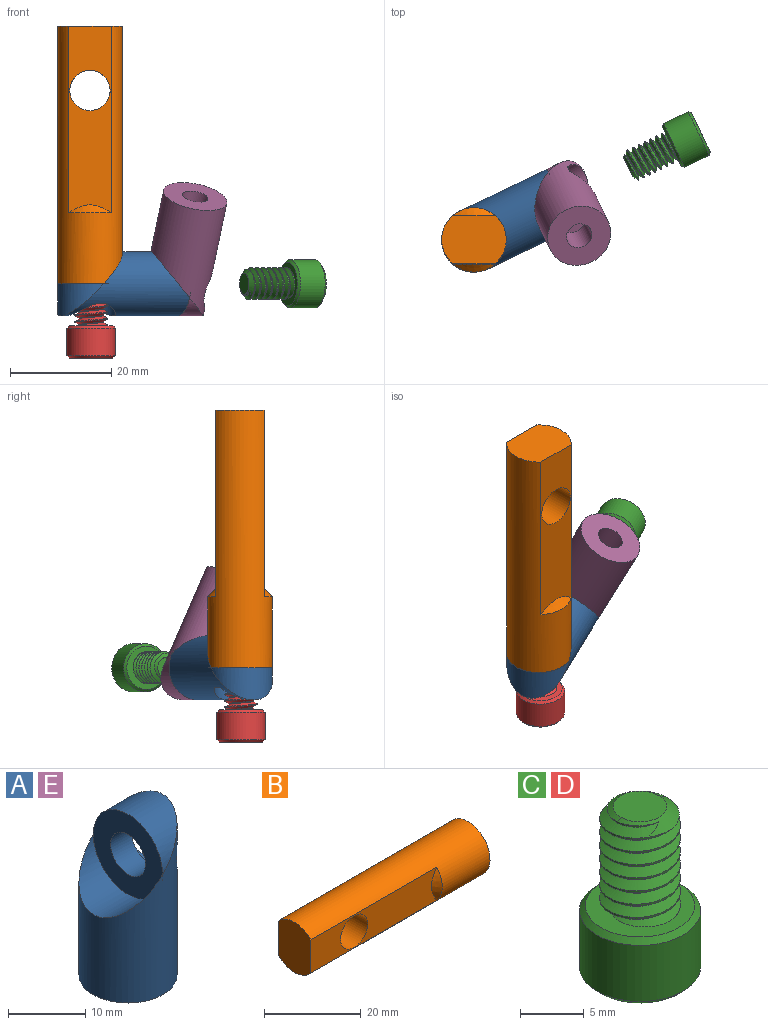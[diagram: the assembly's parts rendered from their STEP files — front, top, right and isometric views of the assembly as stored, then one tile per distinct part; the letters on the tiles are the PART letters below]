
ASSEMBLY  parts=5 mates=4
PART A: 12 faces, bbox 12.7x12.7x25.4 mm
  f0: cylinder r=3.17mm len=6.35mm, axis (-1,0,0), area 76mm2, adj f5,f9
  f1: cylinder r=6.35mm len=25.42mm, axis (0,0,-1), area 670.1mm2, adj f2,f3,f4,f5,f6,f7,f8
  f2: plane 12.7x12.7mm, normal (0,0,-1), area 106.2mm2, adj f1,f10
  f3: cylinder r=6.35mm len=12.7mm, axis (-1,0,0), area 80.6mm2, adj f1,f4,f5
  f4: plane 0.02x0mm, normal (0,0,1), area 0mm2, adj f1,f3
  f5: plane 12.7x12.7mm, normal (-1,0,0), area 95mm2, adj f0,f1,f3,f6
  f6: cylinder r=6.35mm len=12.7mm, axis (-1,0,0), area 80.6mm2, adj f1,f5
  f7: cylinder r=5.08mm len=10.16mm, axis (1,0,0), area 21.5mm2, adj f1,f9
  f8: cylinder r=5.08mm len=10.16mm, axis (1,0,0), area 21.5mm2, adj f1,f9
  f9: plane 10.16x10.16mm, normal (1,0,0), area 49.4mm2, adj f0,f7,f8
  f10: cylinder r=2.55mm len=7.62mm, axis (0,0,-1), area 122.2mm2, adj f2,f11
  f11: plane 5.11x5.11mm, normal (0,0,-1), area 20.5mm2, adj f10
PART B: 10 faces, bbox 50.8x12.7x12.7 mm
  f0: cylinder r=6.35mm len=50.8mm, axis (-1,0,0), area 1350.7mm2, adj f1,f2,f3,f4,f6,f7
  f1: plane 12.7x9.53mm, normal (-1,0,0), area 108.4mm2, adj f0,f3,f4
  f2: plane 12.7x12.7mm, normal (1,0,0), area 106.2mm2, adj f0,f8
  f3: plane 36.83x8.4mm, normal (0,1,0), area 251.3mm2, adj f0,f1,f5,f6
  f4: plane 36.83x8.4mm, normal (0,-1,0), area 251.3mm2, adj f0,f1,f5,f7
  f5: cylinder r=3.97mm len=9.53mm, axis (0,-1,0), area 237.5mm2, adj f3,f4
  f6: cone r=1.27mm half-angle=45deg, axis (1,0,0), area 12.9mm2, adj f0,f3
  f7: cone r=1.27mm half-angle=45deg, axis (1,0,0), area 12.9mm2, adj f0,f4
  f8: cylinder r=2.55mm len=12.7mm, axis (1,0,0), area 203.7mm2, adj f2,f9
  f9: plane 5.11x5.11mm, normal (1,0,0), area 20.5mm2, adj f8
PART C: 54 faces, bbox 10.6x10.6x17.3 mm
  f0: plane 5.5x4.76mm, normal (0,0,-1), area 19.6mm2, adj f1,f49,f50,f51,f52,f53
  f1: plane 4.61x3.42mm, normal (-0.5,0.87,0), area 9.2mm2, adj f0,f2,f49,f53
  f2: revolved ~2.38x1.38mm, area 0mm2, adj f1,f3
  f3: plane 8.58x8.58mm, normal (0,0,-1), area 34mm2, adj f2,f4,f44,f45,f46,f47,f48
  f4: revolved ~9.53x9.53mm, area 19.1mm2, adj f3,f5
  f5: revolved ~9.53x9.53mm, area 161.5mm2, adj f4,f6
  f6: revolved ~9.53x9.53mm, area 19.1mm2, adj f5,f7
  f7: plane 9.07x9.07mm, normal (0,0,1), area 33.5mm2, adj f6,f8,f41,f42,f43
  f8: revolved ~3.18x3.18mm, area 0.6mm2, adj f7,f9,f41,f43
  f9: revolved ~6.35x3.18mm, area 1.6mm2, adj f8,f10,f41,f43
  f10: revolved ~6.35x3.18mm, area 1.6mm2, adj f9,f11,f41,f43
  f11: revolved ~6.35x3.18mm, area 1.6mm2, adj f10,f12,f41,f43
  f12: revolved ~6.35x3.18mm, area 1.6mm2, adj f11,f13,f41,f43
  f13: revolved ~6.35x3.18mm, area 1.6mm2, adj f12,f14,f41,f43
  f14: revolved ~6.35x3.18mm, area 1.6mm2, adj f13,f15,f41,f43
  f15: revolved ~6.35x3.18mm, area 1.6mm2, adj f14,f16,f41,f43
  f16: revolved ~6.35x3.18mm, area 1.6mm2, adj f15,f17,f41,f43
  f17: revolved ~6.35x3.18mm, area 1.6mm2, adj f16,f18,f41,f43
  f18: revolved ~6.35x3.18mm, area 1.6mm2, adj f17,f19,f41,f43
  f19: revolved ~6.35x3.18mm, area 1.6mm2, adj f18,f20,f41,f43
  f20: revolved ~6.35x3.18mm, area 1.6mm2, adj f19,f21,f41,f43
  f21: revolved ~6.35x3.18mm, area 1.6mm2, adj f20,f22,f41,f43
  f22: revolved ~3.8x3.17mm, area 0.7mm2, adj f21,f23,f41,f43
  f23: revolved ~6.35x3.18mm, area 7.1mm2, adj f22,f24,f39,f40,f41,f43
  f24: revolved ~2.34x2.11mm, area 0.4mm2, adj f23,f25,f41,f43
  f25: revolved ~4.7x2.35mm, area 1.2mm2, adj f24,f26,f41,f43
  f26: revolved ~4.7x2.35mm, area 1.2mm2, adj f25,f27,f41,f43
  f27: revolved ~4.7x2.35mm, area 1.2mm2, adj f26,f28,f41,f43
  f28: revolved ~4.7x2.35mm, area 1.2mm2, adj f27,f29,f41,f43
  f29: revolved ~4.7x2.35mm, area 1.2mm2, adj f28,f30,f41,f43
  f30: revolved ~4.7x2.35mm, area 1.2mm2, adj f29,f31,f41,f43
  f31: revolved ~4.7x2.35mm, area 1.2mm2, adj f30,f32,f41,f43
  f32: revolved ~4.7x2.35mm, area 1.2mm2, adj f31,f33,f41,f43
  f33: revolved ~4.7x2.35mm, area 1.2mm2, adj f32,f34,f41,f43
  f34: revolved ~4.7x2.35mm, area 1.2mm2, adj f33,f35,f41,f43
  f35: revolved ~4.7x2.35mm, area 1.2mm2, adj f34,f36,f41,f43
  f36: revolved ~4.7x2.35mm, area 1.2mm2, adj f35,f37,f41,f43
  f37: revolved ~4.7x2.35mm, area 1.2mm2, adj f36,f38,f41,f43
  f38: revolved ~4.7x2.35mm, area 1.2mm2, adj f37,f41,f42,f43
  f39: revolved ~5.91x2.96mm, area 5.7mm2, adj f23,f40,f41
  f40: plane 4.19x4.19mm, normal (0,0,1), area 13.8mm2, adj f23,f39
  f41: bspline ~10.42x7.33mm, area 118.8mm2, adj f7,f8,f9,f10,f11,f12,f13,f14
  f42: revolved ~2.35x2.35mm, area 0.4mm2, adj f7,f38,f41,f43
  f43: bspline ~9.9x7.33mm, area 118mm2, adj f7,f8,f9,f10,f11,f12,f13,f14
  f44: revolved ~2.38x1.38mm, area 0mm2, adj f3,f53
  f45: revolved ~2.75x0.69mm, area 0.7mm2, adj f3,f52
  f46: revolved ~2.38x1.38mm, area 0mm2, adj f3,f51
  f47: revolved ~2.38x1.38mm, area 0mm2, adj f3,f50
  f48: revolved ~2.75x0.37mm, area 0mm2, adj f3,f49
  f49: plane 4.61x3.79mm, normal (-1,0,0), area 9.1mm2, adj f0,f1,f48,f50
  f50: plane 4.61x3.42mm, normal (-0.5,-0.87,0), area 9.2mm2, adj f0,f47,f49,f51
  f51: plane 4.61x3.42mm, normal (0.5,-0.87,0), area 9.2mm2, adj f0,f46,f50,f52
  f52: plane 3.84x3.02mm, normal (1,0,0), area 9.2mm2, adj f0,f45,f51,f53
  f53: plane 4.61x3.42mm, normal (0.5,0.87,0), area 9.2mm2, adj f0,f1,f44,f52
PART D: same geometry as C
PART E: same geometry as A
PLACE A rot(axis=(0.7,0.16,-0.7),161.9deg) t=(8.88,9.26,-57.61)mm
PLACE B rot(axis=(0,1,0),90deg) t=(-8.29,1,-6.81)mm
PLACE C rot(axis=(0.43,-0.9,0),90deg) t=(22.13,15.31,-57.62)mm
PLACE D rot(axis=(0,0,1),25.7deg) t=(-8.06,0.8,-56.37)mm
PLACE E rot(axis=(-0.97,-0.22,0.05),154.9deg) t=(12.46,1.82,-40.44)mm
MATE cylindrical A.f0 <-> D.f7  axis (0,0,-1) through (-8.29,1,-61.42)mm
MATE revolute B.f0 <-> A.f0  axis (0,0,-1) through (-8.29,1,-57.61)mm
MATE revolute A.f1 <-> E.f0  axis (0.9,0.43,0) through (8.88,9.26,-57.61)mm
MATE cylindrical E.f0 <-> C.f7  axis (0.9,0.43,0) through (12.31,10.91,-57.61)mm
